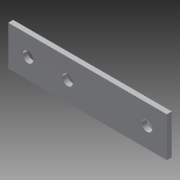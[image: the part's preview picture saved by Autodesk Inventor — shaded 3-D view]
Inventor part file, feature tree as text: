
AUTODESK INVENTOR PART (.ipt)
format: ipt  version: 2014 SP1 (Build 180222100, 222)  size: 84,480 bytes
history: native  units: in
note: dims shown in document units (in); Inventor stores cm internally (conversion verified against a paired STEP export)
features: extrude x1, sketch x1
ambient origin geometry x8: Origin, YZ Plane, XZ Plane, XY Plane, X Axis, Y Axis, Z Axis, Center Point
bodies: Body1 (feature_tree)
feature tree (2):
  extrude  "Extrusion2"  Depth=4.0in
  sketch  "Sketch1"  dims[d0=1.0in d1=4.0in d2=0.266in d3=0.266in d4=0.875in d5=0.5in d6=0.5in d7=0.5in d10=0.266in d11=1.25in d12=0.125in d13=0.0in d14=0.5in]
